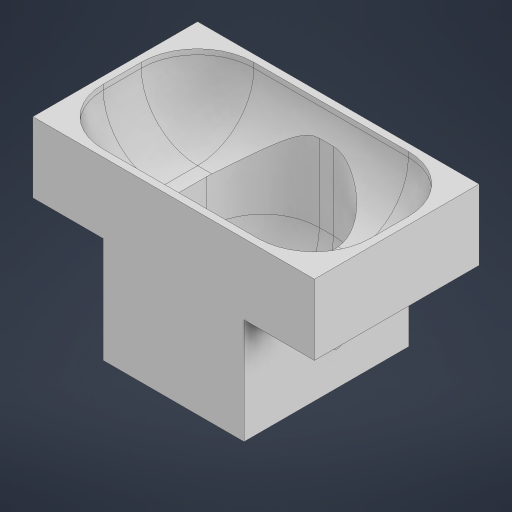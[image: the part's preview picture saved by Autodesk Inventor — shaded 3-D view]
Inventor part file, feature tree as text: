
AUTODESK INVENTOR PART (.ipt)
format: ipt  version: 2023 (Build 270158000, 158)  size: 343,040 bytes
history: native  units: in
note: dims shown in document units (in); Inventor stores cm internally (conversion verified against a paired STEP export)
features: sketch x13, extrude x11, fillet x7
ambient origin geometry x8: Origin, YZ Plane, XZ Plane, XY Plane, X Axis, Y Axis, Z Axis, Center Point
bodies: Solid1 (feature_tree)
feature tree (31):
  sketch  "Sketch1"  dims[d0=3.937in d1=4.6063in]
  extrude  "Extrusion1"  Depth=4.6063in
  sketch  "Sketch3"  dims[d4=4.9213in d5=0.0in d6=3.5433in]
  extrude  "Extrusion2"  Depth=2.3031in
  extrude  "Extrusion3"  Depth=3.5433in
  sketch  "Sketch6"  dims[d9=0.1969in d10=3.5433in]
  extrude  "Extrusion5"  Depth=0.3346in
  extrude  "Extrusion6"  Depth=3.5433in
  extrude  "Extrusion7"  Depth=0.3346in
  fillet  "Face Fillet1"
  fillet  "Face Fillet2"
  fillet  "Face Fillet3"
  fillet  "Face Fillet4"
  extrude  "Extrusion8"  Depth=0.1969in TaperAngle=0.0deg
  extrude  "Extrusion9"  Depth=2.9528in
  extrude  "Extrusion10"  Depth=2.9528in
  extrude  "Extrusion11"  Depth=0.1969in
  extrude  "Extrusion12"  Depth=0.1969in
  fillet  "Face Fillet8"
  fillet  "Face Fillet9"
  fillet  "Face Fillet10"
  sketch  "Sketch2"  dims[d2=1.9685in d3=2.3031in]
  sketch  "Sketch4"  dims[d7=3.937in d8=0.3346in]
  sketch  "Sketch7"  dims[d11=3.937in d12=0.3346in]
  sketch  "Sketch8"  dims[d13=0.1969in d14=0.1969in d15=0.0in]
  sketch  "Sketch9"  dims[d16=4.5276in d17=0.0in d23=2.9528in]
  sketch  "Sketch11"  dims[d24=1.9685in d25=0.0in d26=2.9528in]
  sketch  "Sketch12"  dims[d27=1.9685in d28=0.0in d29=0.1969in]
  sketch  "Sketch13"  dims[d30=0.1969in d31=0.1969in]
  sketch  "Sketch14"  dims[d32=1.7185in d33=0.0in]
  sketch  "Sketch15"  dims[d34=1.5748in d35=1.5748in d36=1.5748in d37=1.5748in d40=0.9449in d43=1.7185in d44=0.0in d48=0.315in d49=2.3031in d50=1.4764in d51=0.1575in d52=0.0in d53=0.315in d54=1.4764in d55=2.3031in d56=0.1575in d57=0.0in d58=0.4331in d59=0.1575in d60=0.0in d61=0.4331in d62=0.1575in d63=0.0in d64=1.7717in d65=0.5118in d66=1.5748in d67=1.5748in d68=1.5748in d18=0.0in d19=0.0in d20=0.0in d21=0.0in d38=0.0in d39=0.0in d69=0.0in d70=0.0in d71=0.0in d72=0.0in]
